# Revit family: Sirius_Three_FS_130kW_150kW_LOD-5
name_source: partatom
category: Mechanical Equipment
units: mm (PartAtom-declared; Revit-internal decimal feet)

## family parameters
Always vertical = Yes
Cut with Voids When Loaded = No
OmniClass Number = 23.75.10.11.14.14
OmniClass Title = Condensing Boilers
Part Type = Normal
Room Calculation Point = No
Round Connector Dimension = Use Diameter
Shared = No
Work Plane-Based = No

## types (2) — shared parameters
6 Monthly = 0
Access Clearance Bottom = 0 mm
Access Clearance Front = 1000 mm
Access Clearance Left = 500 mm
Access Clearance Rear = 500 mm
Access Clearance Right = 500 mm
Access Clearance Top = 400 mm
Air Inlet Connection Size = 160 mm
Annually = As per attached URL O & M Manual
BMS Links = Yes
Bespoke Timeframe = 0
Building Regulations Seasonal Efficiency = 97.3 %
Burner Control Type = Modulating
CE Mark = 0085CP0089
Colour = BDR White (no RAL number)
Condensate Drain Size = 32 mm
Condensate Drain Type = Plain
Configuration = Single boiler
Control Type = 0 - 10V, Volt free enable, Direct boiler weather compensating control system.
Daily = 0
Default Elevation = 0 mm
Drain Connection Size = 0 mm
Drain Connection Type = Plain
Embodied Carbon = 0
Energy Technology List = 0
Environmental Product Declaration = 0
ErP Energy Label = 0
ErP Rated Efficiency at Full Load = 95.1 %
ErP Rated Efficiency at Part Load = 97.8 %
External Material = Steel
Features = Suitable for a range of projects including large domestic properties, small commercial premises and medium to large sized applications that require up to 1mW
Finish = Powder coated
Flow and Return Connection Size = 40 mm
Flow and Return Connection Type = Threaded
Flue Connection size = 110 mm
Flue or Air Intake Classification = B23, B23P, C13,C33, C43, C53, C63, C83
Frequency = 50 Hz
Fuel Connection Size = 25 mm
Fuel Connection Type = Threaded
Full Load Current = 0 A
Fuse Rating = 5 A
Green Guide for Specification = 0
Heat Exchanger Material = Stainless Steel
Heater Operation = Condensing
Hydraulic Resistance at 11C temperature differential = 0.000
Hydraulic Resistance at 15C temperature differential = 0.000
Hydraulic Resistance at 20C temperature differential = 0.410
IK Rating = 0
IP Rating = IP21
IfcExportAs = IfcBoilerType
IfcExportType = NOTDEFINED
Interlocks = Yes
Life Cycle Analysis = 0
Location of Manufacturer = 0
Maintenance Required 0 to 300hrs = 0
Maintenance Required 1001 to 2000hrs = 0
Maintenance Required 2001 to 4000hrs = 0
Maintenance Required 301 to 600hrs = 0
Maintenance Required 4001 to 8000hrs = 0
Maintenance Required 601 to 1000hrs = 0
Maintenance Required 8001 to 12000hrs = 0
Manufacturer = Potterton Commercial
Manufacturer Website = https://www.pottertoncommercial.co.uk
Material Ingredient Reporting = 0
Maximum Gas Inlet Pressure = 0.025 bar
Maximum Oil Inlet Pressure = 0.000 bar
Maximum Operating Pressure = 6.000 bar
Minimum Flow Rate at 11C temperature differential = 0.000 L/s
Minimum Flow Rate at 15C temperature differential = 0.000 L/s
Minimum Gas Inlet Pressure = 0.017 bar
Minimum Oil Inlet Pressure = 0.000 bar
Minimum Operating Pressure = 1.000 bar
Minimum Power Consumption = 0 W
Monthly = 0
Mounting = Floor Standing
Nominal Gas Inlet Pressure = 0.017 bar
Nominal Oil Inlet Pressure = 0.000 bar
Operation and Maintenance Manual = https://www.pottertoncommercial.co.uk
Optional Fuel = Gas - LPG
Overall Height = 1128 mm
Overall Length = 681 mm
Overall Width = 600 mm
Primary Fuel = Gas - NG
Product Literature = https://www.pottertoncommercial.co.uk
Quarterly = 0
Rated Criteria = 50/30
Reference Standard = EU/2016/426 GAR, EN 15502-1, EN15502-2-1
Responsible Extraction of Materials = 0
Responsible Sourcing of Materials = 0
Safety Valve Connection Size = 0 mm
Safety Valve Connection Type = Threaded
Shape = Rectangular (Vertical)
Shipping Weight = 0.00 kg
Starting Current = 0 A
Supply Phase = 1
Turndown Ratio = 5:1
Type = Space heating
Uniclass2015 = Pr_60_60_08_34
Voltage = 230 V
Water Treatment Required = Yes
Weekly = 0
zero-valued in all types: Oil Consumption rate

## per-type parameters (varying)
| type | Expected Life | Gas Consumption rate | Gross Weight | Maximum Power Consumption | Minimum Flow Rate at 20C temperature differential | NOx Emissions | Product Model Number | Product Range | Rated Output | Sound Pressure Level | Water Content |
| 150kW FS | 15 | 15.1 m3/h | 132.00 kg | 283 W | 1.800 L/s | 23 mg/kWh | 7689661 | Sirius Three FS 150kW | 150000 W | 63 dBA | 11.0 L |
| 130kW FS |  | 13.1 m3/h | 126.00 kg | 187 W | 1.560 L/s | 17 mg/kWh | 7689660 | Sirius Three FS 130kW | 130000 W | 63 dB | 10.0 L |

note: source unit labels omitted for Hydraulic Resistance at 11C temperature differential, Hydraulic Resistance at 15C temperature differential, Hydraulic Resistance at 20C temperature differential — the stored unit's dimension contradicts the parameter name (converter mislabeling)

## geometry (parser evidence)
native form markers: Blend x4, Sweep x6
no freeform markers — native parametric forms only
